# Revit family: 9313c4c3-fb8c-42c8-b9a5-083582bd42ef
name_source: partatom
category: Windows
revit_build: Autodesk Revit 2014 (Build: 20130308_1515(x64)
units: mm (PartAtom-declared; Revit-internal decimal feet)

## types (1)
- as Specified
    AAMA Designation = as Specified
    Air Infiltration = as Specified
    Analytic Construction = <None>
    Description = Western Window Combination Aluminum Casement over Awning Pair Window - as Specified
    Expected Lifespan (Years) = 0
    Forced Entry Rating = as Specified
    Frame Depth = 0' - 4 1/2"
    Frame Design_Nail Fin = Yes
    Frame Mounting Setback = 0' - 1"
    Glazing Thickness = 0' - 0 7/8"
    Heat Transfer Coefficient (U) = 1 BTU/(h·ft²·°F)
    Include Screen = Yes
    Keynote = as Specified
    Maintenance Schedule (Months) = 0
    Manufacturer = Western Window Systems
    Manufacturer Fax = 602-243-3119
    Manufacturer Website = https://www.westernwindowsystems.com
    Maximum Size = as Specified
    Meets Egress = as Specified
    Miami Dade Conformance = as Specified
    Model = 670 Combination Pair Awning Casement
    Operation = Awning
    Product Data = http://www.arcat.com
    Product Properties = https://www.westernwindowsystems.com
    R = 1.0000 (h·ft²·°F)/BTU
    RO Spacing_Bottom = 0' - 0"
    RO Spacing_Sides = 0' - 0 1/4"
    RO Spacing_Top = 0' - 0 1/4"
    SHGC = 0
    STC Rating = 0
    Sales Information = https://www.westernwindowsystems.com
    Solar Heat Gain Coefficient = 0
    Standards Conformance = as Specified
    Structural Test Pressure = as Specified
    Thermal Resistance (R) = 1.0000 (h·ft²·°F)/BTU
    U = 1 BTU/(h·ft²·°F)
    URL = https://www.westernwindowsystems.com
    VLT = 0
    Visual Light Transmittance = 0
    Wall Closure = By host
    Warranty Duration (Years) = 0
    Water Penetration = as Specified

## geometry (parser evidence)
native form markers: Sweep x3
no freeform markers — native parametric forms only
